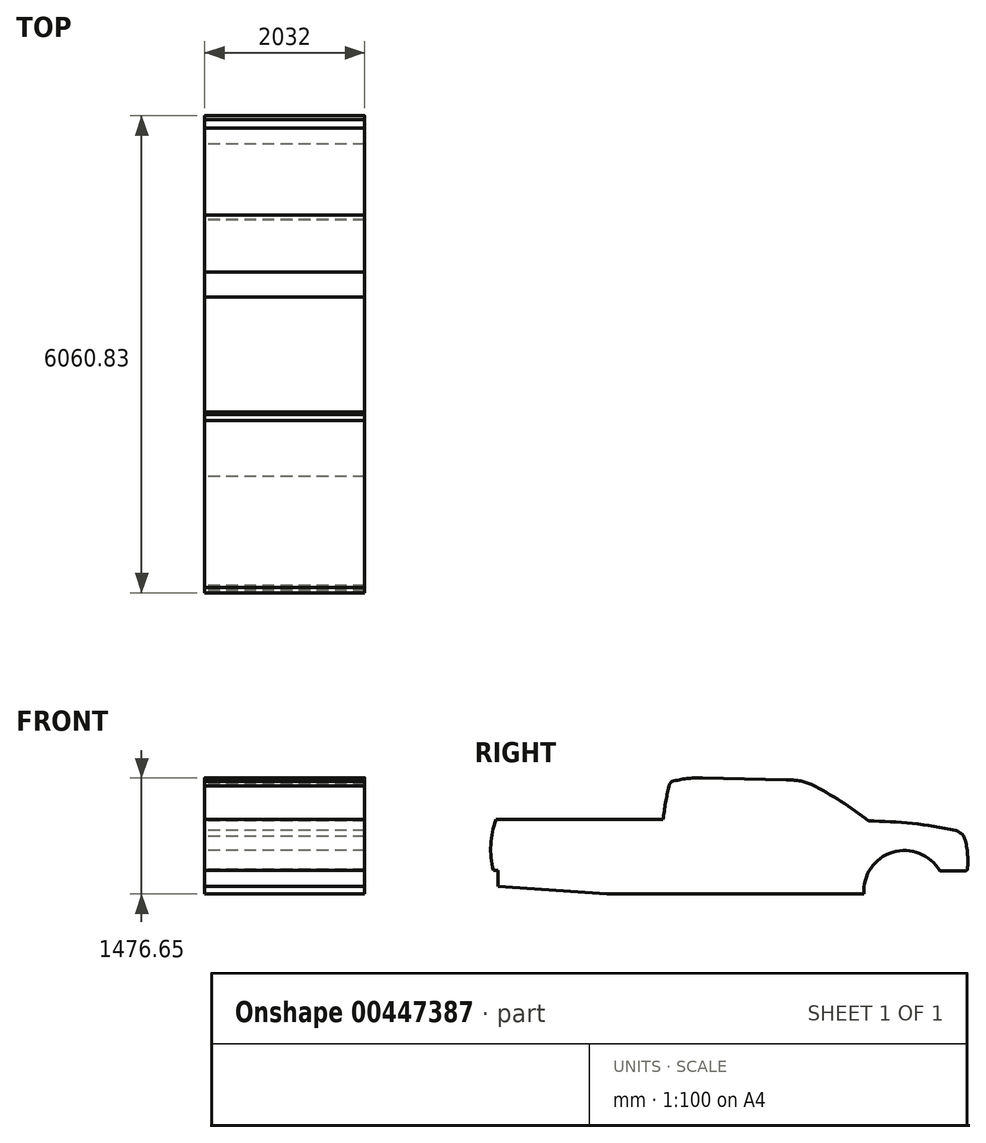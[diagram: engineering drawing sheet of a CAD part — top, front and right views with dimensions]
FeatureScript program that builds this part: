
annotation { "Feature Type Name" : "Feature", "Feature Type Description" : "" }
export const myFeature = defineFeature(function(context is Context, id is Id, definition is map)
    precondition{}
    {
        {
            var Q0;
            Q0=qCreatedBy(makeId("Right.planeOp"),FACE);
            var sketch = newSketch(context, id + "F0", { "sketchPlane" : qUnion([Q0])});
            skLineSegment(sketch, "E0", {"start": v(0, 0) * mm, "end": v(2021.48, 0) * mm});
            skLineSegment(sketch, "E1", {"start": v(0, 0) * mm, "end": v(0, -152.4) * mm});
            skLineSegment(sketch, "E2", {"start": v(0, -152.4) * mm, "end": v(1835.95, -152.4) * mm});
            skLineSegment(sketch, "E3", {"start": v(2042.32, -213.13) * mm, "end": v(2484.5, -498.07) * mm});
            skLineSegment(sketch, "E4", {"start": v(2690.88, -558.8) * mm, "end": v(4358.05, -558.8) * mm});
            skLineSegment(sketch, "E5", {"start": v(4605.7, -467.33) * mm, "end": v(4807.57, -294.67) * mm});
            skLineSegment(sketch, "E6", {"start": v(5055.22, -203.2) * mm, "end": v(5867.18, -203.2) * mm});
            skLineSegment(sketch, "E7", {"start": v(5867.18, -203.2) * mm, "end": v(5867.18, 0) * mm});
            skLineSegment(sketch, "E8", {"start": v(2227.85, -60.73) * mm, "end": v(2551.77, -269.47) * mm});
            skLineSegment(sketch, "E9", {"start": v(2758.15, -330.2) * mm, "end": v(4273.62, -330.2) * mm});
            skLineSegment(sketch, "E10", {"start": v(4521.27, -238.73) * mm, "end": v(4693.45, -91.47) * mm});
            skLineSegment(sketch, "E11.trimOffspring", {"start": v(4941.1, 0) * mm, "end": v(5867.18, 0) * mm});
            skPoint(sketch, "E12.visualSharp", {"position": v(2133.6, 0) * mm});
            skArc(sketch, "E12.filletArc", {"start": v(2227.85, -60.73) * mm, "mid": v(2129.04, -15.5) * mm, "end": v(2021.48, 0) * mm});
            skPoint(sketch, "E13.visualSharp", {"position": v(2646.03, -330.2) * mm});
            skArc(sketch, "E13.filletArc", {"start": v(2551.77, -269.47) * mm, "mid": v(2650.59, -314.7) * mm, "end": v(2758.15, -330.2) * mm});
            skPoint(sketch, "E14.visualSharp", {"position": v(4414.33, -330.2) * mm});
            skArc(sketch, "E14.filletArc", {"start": v(4273.62, -330.2) * mm, "mid": v(4405.62, -306.6) * mm, "end": v(4521.27, -238.73) * mm});
            skPoint(sketch, "E15.visualSharp", {"position": v(4800.38, 0) * mm});
            skArc(sketch, "E15.filletArc", {"start": v(4941.1, 0) * mm, "mid": v(4809.1, -23.6) * mm, "end": v(4693.45, -91.47) * mm});
            skPoint(sketch, "E16.visualSharp", {"position": v(4914.5, -203.2) * mm});
            skArc(sketch, "E16.filletArc", {"start": v(5055.22, -203.2) * mm, "mid": v(4923.22, -226.8) * mm, "end": v(4807.57, -294.67) * mm});
            skPoint(sketch, "E17.visualSharp", {"position": v(4498.76, -558.8) * mm});
            skArc(sketch, "E17.filletArc", {"start": v(4358.05, -558.8) * mm, "mid": v(4490.05, -535.2) * mm, "end": v(4605.7, -467.33) * mm});
            skPoint(sketch, "E18.visualSharp", {"position": v(2578.75, -558.8) * mm});
            skArc(sketch, "E18.filletArc", {"start": v(2484.5, -498.07) * mm, "mid": v(2583.31, -543.3) * mm, "end": v(2690.88, -558.8) * mm});
            skPoint(sketch, "E19.visualSharp", {"position": v(1948.07, -152.4) * mm});
            skArc(sketch, "E19.filletArc", {"start": v(2042.32, -213.13) * mm, "mid": v(1943.51, -167.9) * mm, "end": v(1835.95, -152.4) * mm});
            skSolve(sketch);
        }
        {
            var Q0;
            Q0=qCreatedBy(makeId("Right.planeOp"),FACE);
            var sketch = newSketch(context, id + "F1", { "sketchPlane" : qUnion([Q0])});
            skLineSegment(sketch, "E20", {"start": v(-170.4, 219.3) * mm, "end": v(-170.4, -857.4) * mm});
            skLineSegment(sketch, "E21", {"start": v(6019.58, -198.3) * mm, "end": v(6019.58, 252.37) * mm});
            skLineSegment(sketch, "E22", {"start": v(-19.76, 727.69) * mm, "end": v(2121.8, 727.69) * mm});
            skArc(sketch, "E23", {"start": v(2121.8, 727.69) * mm, "mid": v(2094.9, 253.8) * mm, "end": v(2127.7, -219.7) * mm});
            skLineSegment(sketch, "E24", {"start": v(2127.7, -219.7) * mm, "end": v(1387.88, -219.7) * mm});
            skLineSegment(sketch, "E25", {"start": v(4.83, -122.96) * mm, "end": v(1387.88, -219.7) * mm});
            skArc(sketch, "E26", {"start": v(-19.76, 727.69) * mm, "mid": v(-86.68, 407.29) * mm, "end": v(-55.06, 81.5) * mm});
            skLineSegment(sketch, "E27", {"start": v(-55.06, 81.5) * mm, "end": v(4.83, 81.5) * mm});
            skLineSegment(sketch, "E28", {"start": v(4.83, 81.5) * mm, "end": v(4.83, -122.96) * mm});
            skLineSegment(sketch, "E29", {"start": v(2127.7, -219.7) * mm, "end": v(4651.78, -219.7) * mm});
            skLineSegment(sketch, "E30", {"start": v(5615.56, 74.9) * mm, "end": v(5934.3, 74.9) * mm});
            skArc(sketch, "E31", {"start": v(5615.56, 74.9) * mm, "mid": v(5016.56, 310.72) * mm, "end": v(4651.78, -219.7) * mm});
            skArc(sketch, "E32", {"start": v(5967.01, 94.92) * mm, "mid": v(5967.19, 306.47) * mm, "end": v(5924.24, 513.62) * mm});
            skArc(sketch, "E33", {"start": v(5934.3, 74.9) * mm, "mid": v(5953.48, 80.3) * mm, "end": v(5967.01, 94.92) * mm});
            skArc(sketch, "E34", {"start": v(5924.24, 513.62) * mm, "mid": v(5874.69, 558.13) * mm, "end": v(5817.03, 591.48) * mm});
            skArc(sketch, "E35", {"start": v(5817.03, 591.48) * mm, "mid": v(5267.14, 676.78) * mm, "end": v(4711.7, 710.6) * mm});
            skArc(sketch, "E36", {"start": v(4711.7, 710.6) * mm, "mid": v(4360, 958.36) * mm, "end": v(3986.83, 1172.46) * mm});
            skArc(sketch, "E37", {"start": v(3986.83, 1172.46) * mm, "mid": v(3830.6, 1219) * mm, "end": v(3668.04, 1231.24) * mm});
            skLineSegment(sketch, "E38", {"start": v(3668.04, 1231.24) * mm, "end": v(2598, 1256.57) * mm});
            skArc(sketch, "E39", {"start": v(2598, 1256.57) * mm, "mid": v(2403.4, 1247.26) * mm, "end": v(2212.13, 1210.33) * mm});
            skArc(sketch, "E40", {"start": v(2212.13, 1210.33) * mm, "mid": v(2187.84, 1185.22) * mm, "end": v(2177.32, 1151.91) * mm});
            skArc(sketch, "E41", {"start": v(2177.32, 1151.91) * mm, "mid": v(2082.47, 468.64) * mm, "end": v(2127.7, -219.7) * mm});
            skSolve(sketch);
        }
        {
            var Q0;
            Q0 = qSketchRegion(id + "F1", true);
            extrude(context, id + "F2", {"entities" : qUnion([Q0]), "depth" : 2032 * mm});
        }
    });
